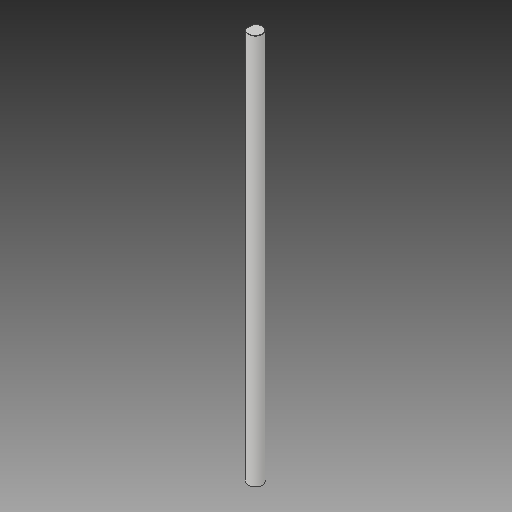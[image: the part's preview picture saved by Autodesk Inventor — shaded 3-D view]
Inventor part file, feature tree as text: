
AUTODESK INVENTOR PART (.ipt)
format: ipt  version: 2017 (Build 210142000, 142)  size: 110,080 bytes
history: native  units: in
note: dims shown in document units (in); Inventor stores cm internally (conversion verified against a paired STEP export)
features: direct_edit x1, chamfer x1, move_body x1
ambient origin geometry x8: Origin, YZ Plane, XZ Plane, XY Plane, X Axis, Y Axis, Z Axis, Center Point
bodies: Solid1 (feature_tree)
feature tree (3):
  direct_edit  "Direct Edit1"
  chamfer  "Chamfer1"  [1 undecoded]
  move_body  "Move1"
note: 1 required parameter value undecoded (feature->parameter linkage not recoverable at this tier; creation-order binding heuristic only, values carry confidence <= 0.55)
